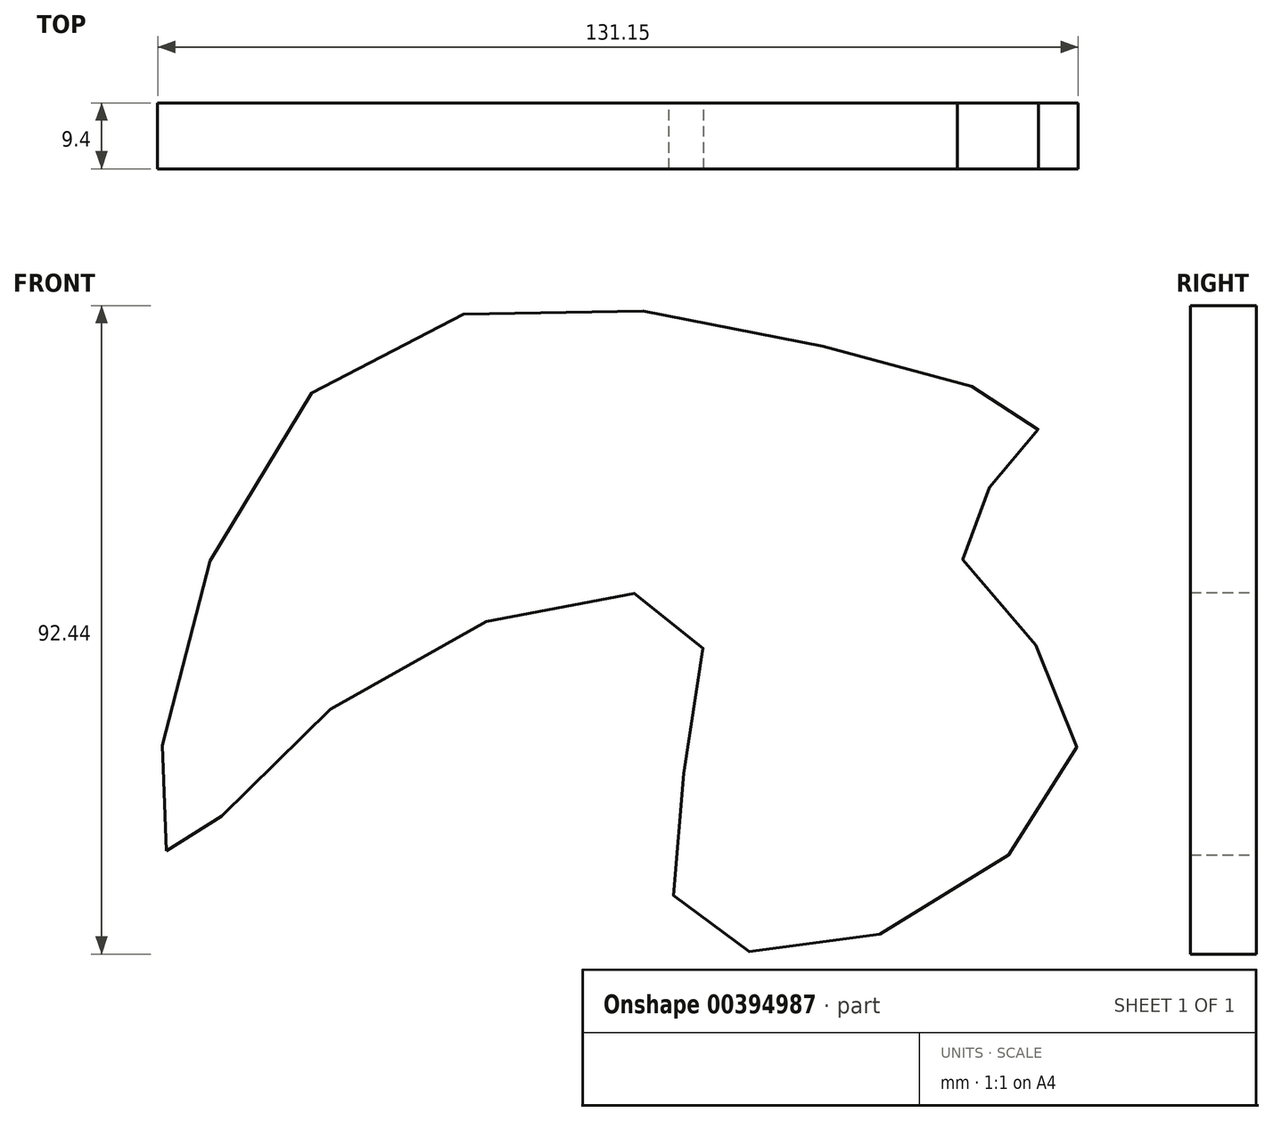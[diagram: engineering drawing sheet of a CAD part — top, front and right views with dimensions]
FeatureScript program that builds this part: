
annotation { "Feature Type Name" : "Feature", "Feature Type Description" : "" }
export const myFeature = defineFeature(function(context is Context, id is Id, definition is map)
    precondition{}
    {
        {
            var Q0;
            Q0=qCreatedBy(makeId("Front.planeOp"),FACE);
            var sketch = newSketch(context, id + "F0", { "sketchPlane" : qUnion([Q0])});
            skFitSpline(sketch, "E0", {"points": [v(-69.61, -9.14) * mm, v(-44.17, 12.7) * mm, v(5.65, 23.54) * mm, v(2.47, -14.83) * mm, v(29.68, -21.82) * mm, v(60.07, 10.27) * mm, v(43.11, 35.77) * mm, v(54.53, 49.98) * mm, v(29.44, 61.44) * mm, v(-48.6, 56.5) * mm, v(-69.61, -9.14) * mm]});
            skSolve(sketch);
        }
        {
            var Q0;
            Q0=makeQuery(id+"F0.imprint","IMPRINT",FACE,{"disambiguationData":[TD([[makeQuery(id+"F0.imprint","IMPRINT",EDGE,{"derivedFrom":sQuery(id+"F0.wireOp",EDGE,"E0")}),1.0]])]});
            extrude(context, id + "F1", {"entities" : qUnion([Q0]), "depth" : 9.4 * mm});
        }
    });
